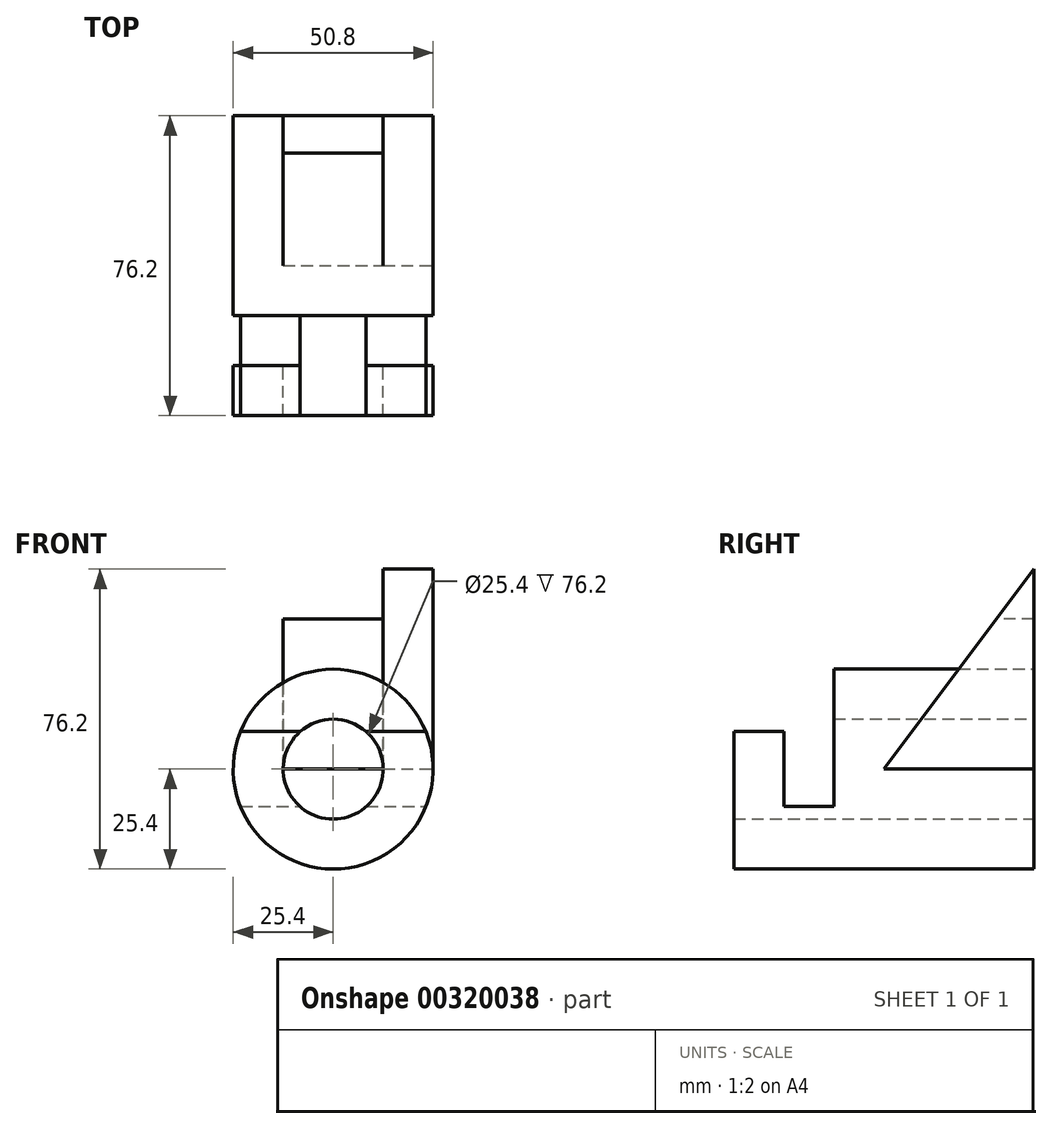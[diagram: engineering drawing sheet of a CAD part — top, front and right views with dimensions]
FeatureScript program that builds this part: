
annotation { "Feature Type Name" : "Feature", "Feature Type Description" : "" }
export const myFeature = defineFeature(function(context is Context, id is Id, definition is map)
    precondition{}
    {
        {
            var Q0;
            Q0=qCreatedBy(makeId("Front.planeOp"),FACE);
            var sketch = newSketch(context, id + "F0", { "sketchPlane" : qUnion([Q0])});
            skCircle(sketch, "E0", {"center": v(0, 0) * mm, "radius": 12.7 * mm});
            skCircle(sketch, "E1", {"center": v(0, 0) * mm, "radius": 25.4 * mm});
            skSolve(sketch);
        }
        {
            var Q0;
            Q0 = qSketchRegion(id + "F0", true);
            extrude(context, id + "F1", {"entities" : qUnion([Q0]), "depth" : 50.8 * mm});
        }
        {
            var Q0;
            Q0=qCreatedBy(makeId("Right.planeOp"),FACE);
            cPlane(context, id + "F2", {"entities" : qUnion([Q0]), "cplaneType" : CPlaneType.OFFSET, "offset" : 25.4 * mm, "width" : 152.4 * mm, "height" : 152.4 * mm});
        }
        {
            var Q0;
            Q0=qCreatedBy(id+"F2.planeOp",FACE);
            var sketch = newSketch(context, id + "F3", { "sketchPlane" : qUnion([Q0])});
            skLineSegment(sketch, "E2", {"start": v(0, 0) * mm, "end": v(0, 50.8) * mm});
            skLineSegment(sketch, "E3", {"start": v(0, 50.8) * mm, "end": v(-38.1, 0) * mm});
            skLineSegment(sketch, "E4", {"start": v(-38.1, 0) * mm, "end": v(0, 0) * mm});
            skSolve(sketch);
        }
        {
            var Q0;
            Q0 = qSketchRegion(id + "F3", true);
            extrude(context, id + "F4", {"entities" : qUnion([Q0]), "oppositeDirection" : true, "depth" : 12.7 * mm});
        }
        {
            var Q0;
            Q0=makeQuery(id+"F4.opExtrude","CAP_FACE",FACE,{"disambiguationData":[OSD([sQuery(id+"F3.wireOp",EDGE,"E2"),sQuery(id+"F3.wireOp",EDGE,"E3"),sQuery(id+"F3.wireOp",EDGE,"E4")])],"isStart":false});
            var sketch = newSketch(context, id + "F5", { "sketchPlane" : qUnion([Q0])});
            skLineSegment(sketch, "E5", {"start": v(0, 0) * mm, "end": v(0, 38.1) * mm});
            skLineSegment(sketch, "E6", {"start": v(0, 38.1) * mm, "end": v(9.52, 38.1) * mm});
            skLineSegment(sketch, "E7", {"start": v(9.52, 38.1) * mm, "end": v(38.1, 0) * mm});
            skLineSegment(sketch, "E8", {"start": v(38.1, 0) * mm, "end": v(0, 0) * mm});
            skSolve(sketch);
        }
        {
            var Q0;
            Q0 = qSketchRegion(id + "F5", true);
            extrude(context, id + "F6", {"entities" : qUnion([Q0]), "depth" : 25.4 * mm});
        }
        {
            var Q0;
            Q0=makeQuery(id+"F1.opExtrude","CAP_FACE",FACE,{"disambiguationData":[OSD([sQuery(id+"F0.wireOp",EDGE,"E0"),sQuery(id+"F0.wireOp",EDGE,"E1")])],"isStart":false});
            var sketch = newSketch(context, id + "F7", { "sketchPlane" : qUnion([Q0])});
            skArc(sketch, "E9", {"start": v(-8.4, -9.53) * mm, "mid": v(0, -12.7) * mm, "end": v(8.4, -9.53) * mm});
            skArc(sketch, "E10", {"start": v(-23.55, -9.52) * mm, "mid": v(0, -25.4) * mm, "end": v(23.55, -9.53) * mm});
            skLineSegment(sketch, "E11", {"start": v(-23.55, -9.53) * mm, "end": v(-8.4, -9.53) * mm});
            skLineSegment(sketch, "E12.trimOffspring", {"start": v(8.4, -9.53) * mm, "end": v(23.55, -9.53) * mm});
            skSolve(sketch);
        }
        {
            var Q0;
            Q0 = qSketchRegion(id + "F7", true);
            extrude(context, id + "F8", {"entities" : qUnion([Q0]), "operationType" : NewBodyOperationType.ADD, "depth" : 12.7 * mm});
        }
        {
            var Q0;
            Q0=makeQuery(id+"F8.opExtrude","CAP_FACE",FACE,{"disambiguationData":[OSD([sQuery(id+"F7.wireOp",EDGE,"E9"),sQuery(id+"F7.wireOp",EDGE,"E10"),sQuery(id+"F7.wireOp",EDGE,"E11"),sQuery(id+"F7.wireOp",EDGE,"E12.trimOffspring")])],"isStart":false});
            var sketch = newSketch(context, id + "F9", { "sketchPlane" : qUnion([Q0])});
            skArc(sketch, "E13", {"start": v(-8.4, 9.53) * mm, "mid": v(0, -12.7) * mm, "end": v(8.4, 9.52) * mm});
            skArc(sketch, "E14", {"start": v(-23.55, 9.52) * mm, "mid": v(0, -25.4) * mm, "end": v(23.55, 9.52) * mm});
            skLineSegment(sketch, "E15", {"start": v(-23.55, 9.53) * mm, "end": v(-8.4, 9.53) * mm});
            skLineSegment(sketch, "E16.trimOffspring", {"start": v(8.4, 9.53) * mm, "end": v(23.55, 9.53) * mm});
            skSolve(sketch);
        }
        {
            var Q0;
            Q0 = qSketchRegion(id + "F9", true);
            extrude(context, id + "F10", {"entities" : qUnion([Q0]), "operationType" : NewBodyOperationType.ADD, "depth" : 12.7 * mm});
        }
    });
